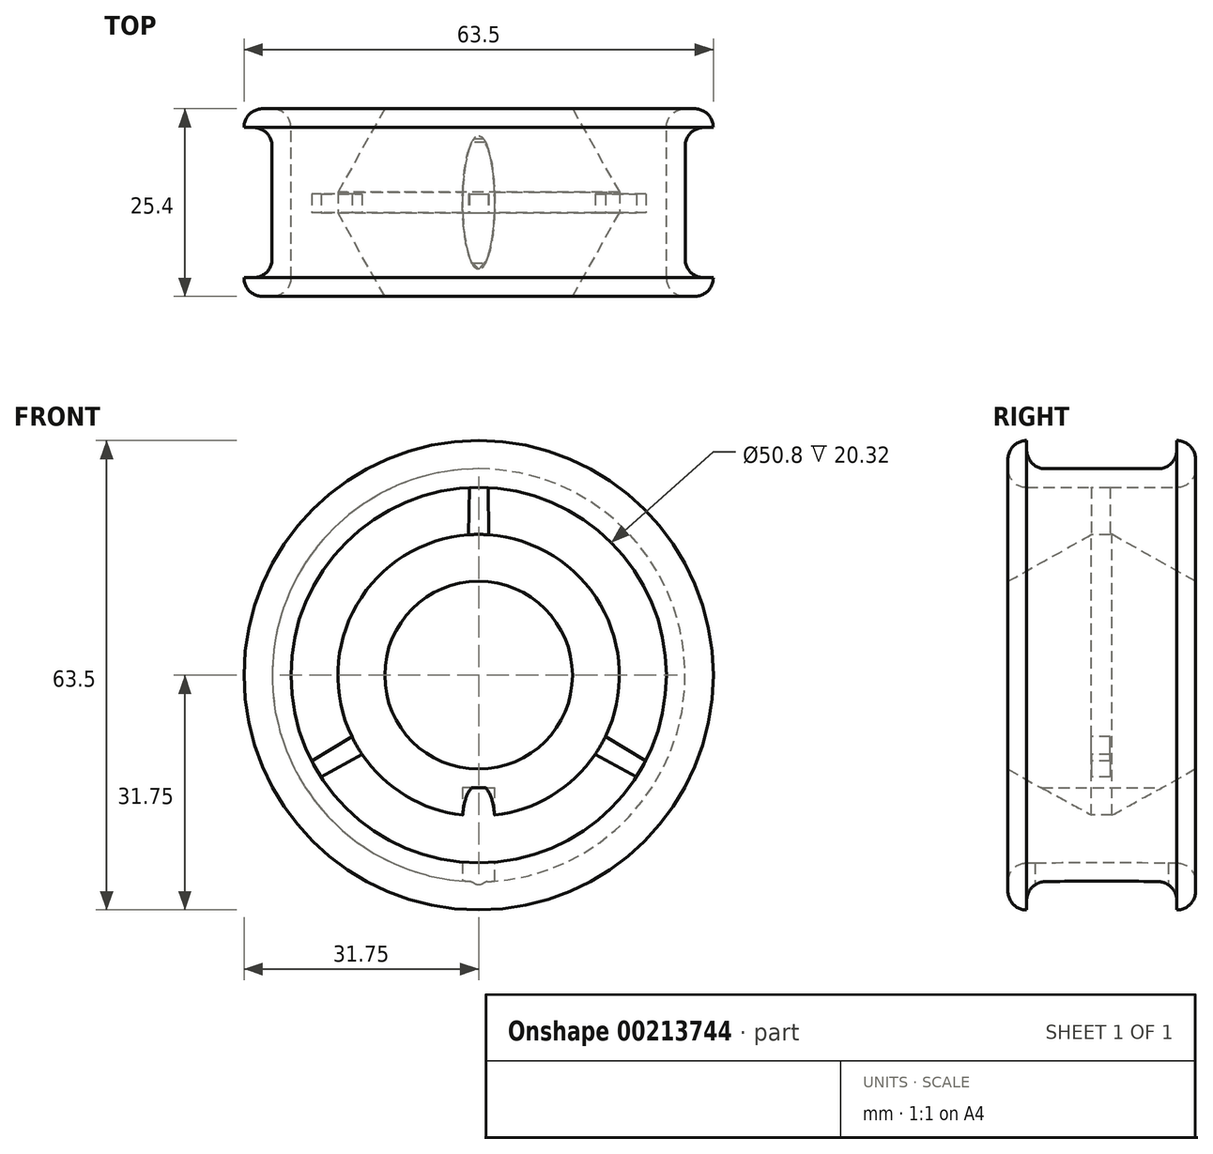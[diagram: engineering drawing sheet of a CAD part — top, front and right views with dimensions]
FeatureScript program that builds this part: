
annotation { "Feature Type Name" : "Feature", "Feature Type Description" : "" }
export const myFeature = defineFeature(function(context is Context, id is Id, definition is map)
    precondition{}
    {
        {
            var Q0;
            Q0=qCreatedBy(makeId("Top.planeOp"),FACE);
            var sketch = newSketch(context, id + "F0", { "sketchPlane" : qUnion([Q0])});
            skLineSegment(sketch, "E0", {"start": v(0, 0) * mm, "end": v(-31.75, 0) * mm, "construction": true});
            skLineSegment(sketch, "E1", {"start": v(-31.75, 12.7) * mm, "end": v(-31.75, 10.16) * mm});
            skLineSegment(sketch, "E2", {"start": v(-31.75, -12.7) * mm, "end": v(-25.4, -12.7) * mm});
            skLineSegment(sketch, "E3", {"start": v(-25.4, -12.7) * mm, "end": v(-25.4, 12.7) * mm, "construction": true});
            skLineSegment(sketch, "E4", {"start": v(-25.4, 12.7) * mm, "end": v(-31.75, 12.7) * mm});
            skLineSegment(sketch, "E5.bottom", {"start": v(0, 12.7) * mm, "end": v(-12.7, 12.7) * mm});
            skLineSegment(sketch, "E5.top", {"start": v(0, -12.7) * mm, "end": v(-12.7, -12.7) * mm});
            skLineSegment(sketch, "E5.left", {"start": v(0, 12.7) * mm, "end": v(0, -12.7) * mm});
            skLineSegment(sketch, "E6", {"start": v(-25.4, 12.7) * mm, "end": v(-25.4, 1.4) * mm});
            skLineSegment(sketch, "E7", {"start": v(-25.4, 1.4) * mm, "end": v(-19.05, 1.4) * mm});
            skLineSegment(sketch, "E8", {"start": v(-25.4, -1.4) * mm, "end": v(-25.4, -12.7) * mm});
            skLineSegment(sketch, "E9", {"start": v(-25.4, -1.4) * mm, "end": v(-19.05, -1.4) * mm});
            skLineSegment(sketch, "E10", {"start": v(-19.05, 1.4) * mm, "end": v(-12.7, 12.7) * mm});
            skLineSegment(sketch, "E11", {"start": v(-12.7, -12.7) * mm, "end": v(-19.05, -1.4) * mm});
            skLineSegment(sketch, "E12", {"start": v(-19.05, 1.4) * mm, "end": v(-19.05, -1.4) * mm, "construction": true});
            skLineSegment(sketch, "E13", {"start": v(-12.7, 12.7) * mm, "end": v(-12.7, -12.7) * mm, "construction": true});
            skLineSegment(sketch, "E14", {"start": v(-31.75, 10.16) * mm, "end": v(-27.94, 10.16) * mm});
            skLineSegment(sketch, "E15", {"start": v(-27.94, 10.16) * mm, "end": v(-27.94, -10.16) * mm});
            skLineSegment(sketch, "E16", {"start": v(-27.94, -10.16) * mm, "end": v(-31.75, -10.16) * mm});
            skLineSegment(sketch, "E17.trimOffspring", {"start": v(-31.75, -10.16) * mm, "end": v(-31.75, -12.7) * mm});
            skSolve(sketch);
        }
        {
            var Q0;
            Q0 = qSketchRegion(id + "F0", true);
            var Q1;
            Q1=sQuery(id+"F0.wireOp",EDGE,"E5.left");
            revolve(context, id + "F1", {"entities" : qUnion([Q0]), "axis" : qUnion([Q1]), "revolveType" : RevolveType.FULL});
        }
        {
            var Q0;
            Q0=makeQuery(id+"F1.opRevolve","SWEPT_FACE",FACE,{"disambiguationData":[OSD([sQuery(id+"F0.wireOp",EDGE,"E9")])]});
            var sketch = newSketch(context, id + "F2", { "sketchPlane" : qUnion([Q0])});
            skLineSegment(sketch, "E18", {"start": v(0, 0) * mm, "end": v(0, 25.4) * mm, "construction": true});
            skLineSegment(sketch, "E19", {"start": v(-1.27, 25.37) * mm, "end": v(-1.38, 19) * mm});
            skLineSegment(sketch, "E20", {"start": v(-1.38, 19) * mm, "end": v(1.38, 19) * mm, "construction": true});
            skLineSegment(sketch, "E21", {"start": v(1.38, 19) * mm, "end": v(1.27, 25.37) * mm});
            skLineSegment(sketch, "E22", {"start": v(1.27, 25.37) * mm, "end": v(-1.27, 25.37) * mm, "construction": true});
            skArc(sketch, "E23", {"start": v(1.38, 19) * mm, "mid": v(0, 19.05) * mm, "end": v(-1.38, 19) * mm});
            skArc(sketch, "E24", {"start": v(-1.27, 25.37) * mm, "mid": v(0, 25.4) * mm, "end": v(1.27, 25.37) * mm});
            skSolve(sketch);
        }
        {
            var Q0;
            {var subQ0=sQuery(id+"F2.wireOp",EDGE,"E19");Q0=makeQuery(id+"F2.imprint","IMPRINT",FACE,{"disambiguationData":[TD([[makeQuery(id+"F2.imprint","IMPRINT",EDGE,{"derivedFrom":subQ0}),-1.0]])]});}
            var sketch = newSketch(context, id + "F3", { "sketchPlane" : qUnion([Q0])});
            skCircle(sketch, "E25", {"center": v(0, 0) * mm, "radius": 19.05 * mm});
            skCircle(sketch, "E26", {"center": v(0, 0) * mm, "radius": 25.4 * mm});
            skSolve(sketch);
        }
        {
            var Q0;
            Q0 = qSketchRegion(id + "F3", true);
            extrude(context, id + "F4", {"entities" : qUnion([Q0]), "operationType" : NewBodyOperationType.REMOVE, "endBound" : BoundingType.THROUGH_ALL, "oppositeDirection" : true, "depth" : 25.4 * mm});
        }
        {
            var Q0;
            Q0 = qSketchRegion(id + "F2", true);
            extrude(context, id + "F5", {"entities" : qUnion([Q0]), "oppositeDirection" : true, "depth" : 2.54 * mm});
        }
        {
            var Q0;
            Q0=makeQuery(id+"F5.opExtrude","SWEPT_BODY",BODY,{"disambiguationData":[OSD([sQuery(id+"F2.wireOp",EDGE,"E19"),sQuery(id+"F2.wireOp",EDGE,"E21"),sQuery(id+"F2.wireOp",EDGE,"E23"),sQuery(id+"F2.wireOp",EDGE,"E24")])]});
            var Q1;
            Q1=makeQuery(id+"F4.boolean.opBoolean","MERGE",EDGE,{"derivedFrom":[makeQuery(id+"F1.opRevolve","SWEPT_EDGE",EDGE,{"disambiguationData":[OSD([sQuery(id+"F0.wireOp",EDGE,"E9"),sQuery(id+"F0.wireOp",EDGE,"E11")])]}),makeQuery(id+"F4.opExtrude","CAP_EDGE",EDGE,{"disambiguationData":[OSD([sQuery(id+"F3.wireOp",EDGE,"E25")])],"isStart":true})]});
            circularPattern(context, id + "F6", {"operationType" : NewBodyOperationType.ADD, "entities" : qUnion([Q0]), "axis" : qUnion([Q1]), "angle" : 360 * degree, "instanceCount" : 3, "equalSpace" : true});
        }
        {
            var Q0;
            Q0=qCreatedBy(makeId("Top.planeOp"),FACE);
            cPlane(context, id + "F7", {"entities" : qUnion([Q0]), "cplaneType" : CPlaneType.OFFSET, "offset" : 31.75 * mm, "oppositeDirection" : true, "width" : 152.4 * mm, "height" : 152.4 * mm});
        }
        {
            var Q0;
            Q0=qCreatedBy(id+"F7.planeOp",FACE);
            var sketch = newSketch(context, id + "F8", { "sketchPlane" : qUnion([Q0])});
            skEllipse(sketch, "E27", {"center": v(0, 0) * mm, "majorRadius": 9.03 * mm, "minorRadius": 2.18 * mm, "majorAxis": v(0, -1)});
            skSolve(sketch);
        }
        {
            var Q0;
            Q0 = qSketchRegion(id + "F8", true);
            extrude(context, id + "F9", {"entities" : qUnion([Q0]), "operationType" : NewBodyOperationType.REMOVE, "depth" : 16.5 * mm});
        }
        {
            var Q0;
            Q0=makeQuery(id+"F1.opRevolve","SWEPT_EDGE",EDGE,{"disambiguationData":[OSD([sQuery(id+"F0.wireOp",EDGE,"E15"),sQuery(id+"F0.wireOp",EDGE,"E16")])]});
            var Q1;
            Q1=makeQuery(id+"F1.opRevolve","SWEPT_EDGE",EDGE,{"disambiguationData":[OSD([sQuery(id+"F0.wireOp",EDGE,"E14"),sQuery(id+"F0.wireOp",EDGE,"E15")])]});
            var Q2;
            Q2=makeQuery(id+"F6.opPattern","COPY",EDGE,{"derivedFrom":makeQuery(id+"F5.opExtrude","CAP_EDGE",EDGE,{"disambiguationData":[OSD([sQuery(id+"F2.wireOp",EDGE,"E24")])],"isStart":true}),"instanceName":"2"});
            var Q3;
            Q3=makeQuery(id+"F6.opPattern","COPY",EDGE,{"derivedFrom":makeQuery(id+"F5.opExtrude","SWEPT_EDGE",EDGE,{"disambiguationData":[OSD([sQuery(id+"F0.wireOp",EDGE,"E8"),sQuery(id+"F0.wireOp",EDGE,"E9"),sQuery(id+"F2.wireOp",EDGE,"E21"),sQuery(id+"F2.wireOp",EDGE,"E24")])]}),"instanceName":"2"});
            var Q4;
            Q4=makeQuery(id+"F6.opPattern","COPY",EDGE,{"derivedFrom":makeQuery(id+"F5.opExtrude","SWEPT_EDGE",EDGE,{"disambiguationData":[OSD([sQuery(id+"F0.wireOp",EDGE,"E8"),sQuery(id+"F0.wireOp",EDGE,"E9"),sQuery(id+"F2.wireOp",EDGE,"E19"),sQuery(id+"F2.wireOp",EDGE,"E24")])]}),"instanceName":"2"});
            var Q5;
            Q5=makeQuery(id+"F6.opPattern","COPY",EDGE,{"derivedFrom":makeQuery(id+"F5.opExtrude","CAP_EDGE",EDGE,{"disambiguationData":[OSD([sQuery(id+"F2.wireOp",EDGE,"E24")])],"isStart":false}),"instanceName":"2"});
            var Q6;
            Q6=makeQuery(id+"F6.opPattern","COPY",EDGE,{"derivedFrom":makeQuery(id+"F5.opExtrude","CAP_EDGE",EDGE,{"disambiguationData":[OSD([sQuery(id+"F2.wireOp",EDGE,"E24")])],"isStart":false}),"instanceName":"1"});
            var Q7;
            Q7=makeQuery(id+"F6.opPattern","COPY",EDGE,{"derivedFrom":makeQuery(id+"F5.opExtrude","SWEPT_EDGE",EDGE,{"disambiguationData":[OSD([sQuery(id+"F0.wireOp",EDGE,"E8"),sQuery(id+"F0.wireOp",EDGE,"E9"),sQuery(id+"F2.wireOp",EDGE,"E19"),sQuery(id+"F2.wireOp",EDGE,"E24")])]}),"instanceName":"1"});
            var Q8;
            Q8=makeQuery(id+"F6.opPattern","COPY",EDGE,{"derivedFrom":makeQuery(id+"F5.opExtrude","SWEPT_EDGE",EDGE,{"disambiguationData":[OSD([sQuery(id+"F0.wireOp",EDGE,"E8"),sQuery(id+"F0.wireOp",EDGE,"E9"),sQuery(id+"F2.wireOp",EDGE,"E21"),sQuery(id+"F2.wireOp",EDGE,"E24")])]}),"instanceName":"1"});
            var Q9;
            Q9=makeQuery(id+"F6.opPattern","COPY",EDGE,{"derivedFrom":makeQuery(id+"F5.opExtrude","CAP_EDGE",EDGE,{"disambiguationData":[OSD([sQuery(id+"F2.wireOp",EDGE,"E24")])],"isStart":true}),"instanceName":"1"});
            var Q10;
            Q10=makeQuery(id+"F5.opExtrude","CAP_EDGE",EDGE,{"disambiguationData":[OSD([sQuery(id+"F2.wireOp",EDGE,"E24")])],"isStart":true});
            var Q11;
            Q11=makeQuery(id+"F5.opExtrude","SWEPT_EDGE",EDGE,{"disambiguationData":[OSD([sQuery(id+"F0.wireOp",EDGE,"E8"),sQuery(id+"F0.wireOp",EDGE,"E9"),sQuery(id+"F2.wireOp",EDGE,"E19"),sQuery(id+"F2.wireOp",EDGE,"E24")])]});
            var Q12;
            Q12=makeQuery(id+"F5.opExtrude","SWEPT_EDGE",EDGE,{"disambiguationData":[OSD([sQuery(id+"F0.wireOp",EDGE,"E8"),sQuery(id+"F0.wireOp",EDGE,"E9"),sQuery(id+"F2.wireOp",EDGE,"E21"),sQuery(id+"F2.wireOp",EDGE,"E24")])]});
            var Q13;
            Q13=makeQuery(id+"F5.opExtrude","CAP_EDGE",EDGE,{"disambiguationData":[OSD([sQuery(id+"F2.wireOp",EDGE,"E24")])],"isStart":false});
            fillet(context, id + "F10", {"entities" : qUnion([Q0, Q1, Q2, Q3, Q4, Q5, Q6, Q7, Q8, Q9, Q10, Q11, Q12, Q13]), "radius" : 2.54 * mm, "tangentPropagation" : true, "allowEdgeOverflow" : false});
        }
        {
            var Q0;
            Q0=makeQuery(id+"F1.opRevolve","SWEPT_FACE",FACE,{"disambiguationData":[OSD([sQuery(id+"F0.wireOp",EDGE,"E4")])]});
            var Q1;
            Q1=makeQuery(id+"F1.opRevolve","SWEPT_FACE",FACE,{"disambiguationData":[OSD([sQuery(id+"F0.wireOp",EDGE,"E2")])]});
            fillet(context, id + "F11", {"entities" : qUnion([Q0, Q1]), "radius" : 2.54 * mm, "tangentPropagation" : true, "allowEdgeOverflow" : false});
        }
    });
